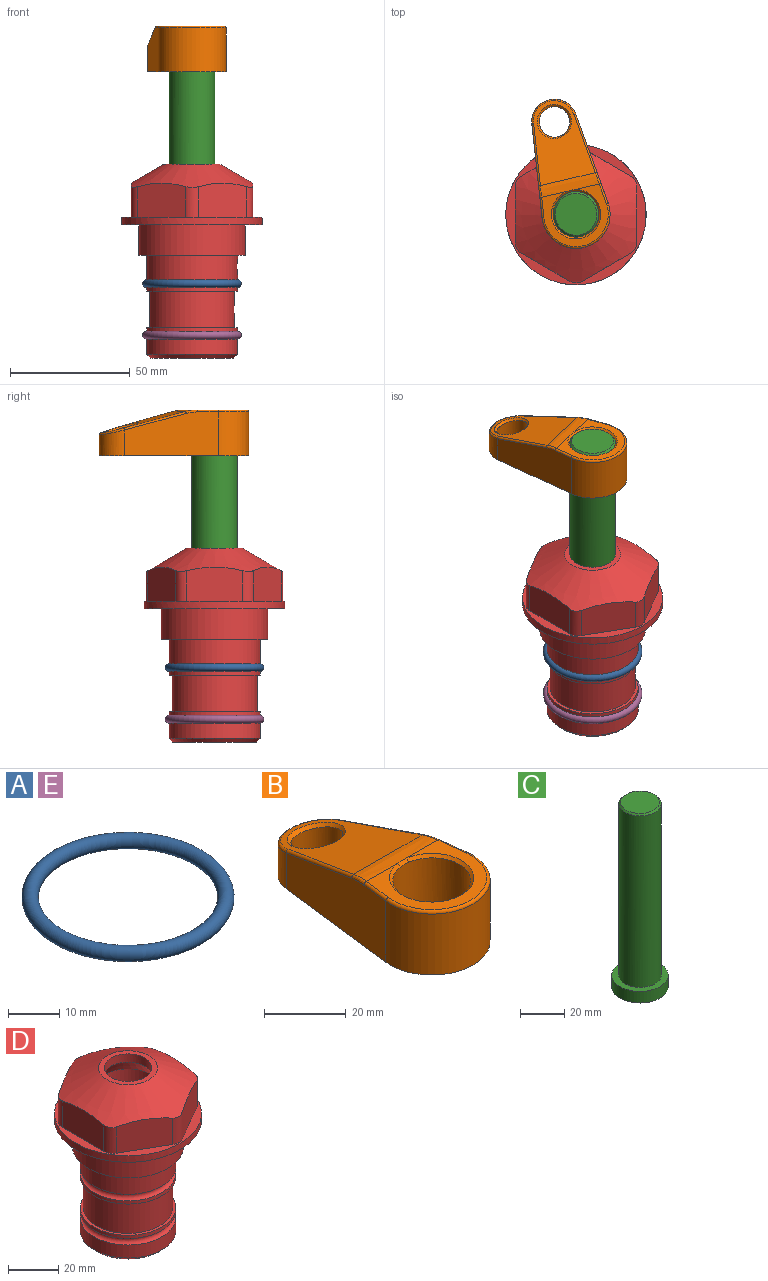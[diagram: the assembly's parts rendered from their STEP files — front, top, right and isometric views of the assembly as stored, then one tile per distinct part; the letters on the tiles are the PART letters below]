
ASSEMBLY  parts=5 mates=4
PART A: 1 faces, bbox 44.7x44.7x3.2 mm
  f0: torus R=19.05mm, axis (0,0,1), area 1193.9mm2
PART B: 31 faces, bbox 31.7x65.5x19.8 mm
  f0: plane 39.12x18.26mm, normal (0.99,0.12,0), area 612.2mm2, adj f1,f4,f7,f11,f13,f15
  f1: cylinder r=9.53mm len=18.91mm, axis (0,0,-1), area 296.1mm2, adj f0,f2,f7,f17
  f2: plane 39.12x18.26mm, normal (-0.99,0.12,0), area 612.2mm2, adj f1,f4,f7,f12,f14,f16
  f3: cylinder r=6.35mm len=12.7mm, axis (0,0,-1), area 362.4mm2, adj f7,f18
  f4: cylinder r=14.29mm len=28.58mm, axis (0,0,-1), area 882.2mm2, adj f0,f2,f7,f10
  f5: cylinder r=9.53mm len=19.05mm, axis (0,0,-1), area 1092.6mm2, adj f7,f19,f20
  f6: plane 26.99x23.69mm, normal (0,0,1), area 216.2mm2, adj f9,f10,f11,f12,f19
  f7: plane 63.5x28.58mm, normal (0,0,-1), area 661.8mm2, adj f0,f1,f2,f3,f4,f5,f22,f23
  f8: plane 33.52x23.6mm, normal (0,0.26,0.97), area 486mm2, adj f9,f15,f16,f17,f18
  f9: cylinder r=19.05mm len=24.72mm, axis (1,0,0), area 120.4mm2, adj f6,f8,f13,f14,f20
  f10: torus R=13.49mm, axis (0,0,1), area 59mm2, adj f4,f6,f11,f12
  f11: cylinder r=0.79mm len=8.67mm, axis (0.12,-0.99,0), area 10.8mm2, adj f0,f6,f10,f13
  f12: cylinder r=0.79mm len=8.67mm, axis (0.12,0.99,0), area 10.8mm2, adj f2,f6,f10,f14
  f13: bspline ~4.95x1.42mm, area 6.1mm2, adj f0,f9,f11,f15
  f14: bspline ~4.95x1.42mm, area 6.1mm2, adj f2,f9,f12,f16
  f15: cylinder r=0.79mm len=25.95mm, axis (0.12,-0.96,0.26), area 32.9mm2, adj f0,f8,f13,f17
  f16: cylinder r=0.79mm len=25.95mm, axis (0.12,0.96,-0.26), area 32.9mm2, adj f2,f8,f14,f17
  f17: bspline ~18.91x8.38mm, area 30mm2, adj f1,f8,f15,f16
  f18: bspline ~14.29x14.29mm, area 48.3mm2, adj f3,f8
  f19: cone r=9.53mm half-angle=45deg, axis (0,0,1), area 66.5mm2, adj f5,f6,f20
  f20: bspline ~3.22x0.96mm, area 3.5mm2, adj f5,f9,f19
  f21: plane 2.75x2.72mm, normal (0,0,-1), area 2.9mm2, adj f23,f25,f28
  f22: plane 23.05x15.88mm, normal (-0.99,-0.12,0), area 323.6mm2, adj f7,f25,f26,f27,f28,f29
  f23: plane 23.05x15.88mm, normal (0.99,-0.12,0), area 323.6mm2, adj f7,f21,f25,f27,f28,f30
  f24: cylinder r=9.53mm len=10.69mm, axis (0,0,-1), area 114.7mm2, adj f7,f27,f29,f30
  f25: cylinder r=12.7mm len=20.59mm, axis (0,0,-1), area 381.1mm2, adj f7,f21,f22,f23,f26,f28
  f26: plane 2.75x2.72mm, normal (0,0,-1), area 2.9mm2, adj f22,f25,f28
  f27: plane 19.72x18.37mm, normal (0,-0.26,-0.97), area 291.8mm2, adj f22,f23,f24,f28,f29,f30
  f28: cylinder r=15.88mm len=19.92mm, axis (1,0,0), area 54.8mm2, adj f21,f22,f23,f25,f26,f27
  f29: cylinder r=1.59mm len=11mm, axis (0,0,-1), area 34.7mm2, adj f7,f22,f24,f27
  f30: cylinder r=1.59mm len=11mm, axis (0,0,-1), area 34.7mm2, adj f7,f23,f24,f27
PART C: 6 faces, bbox 25.4x25.4x101.6 mm
  f0: plane 17.46x17.46mm, normal (0,0,1), area 239.5mm2, adj f5
  f1: plane 25.4x25.4mm, normal (0,0,-1), area 506.7mm2, adj f2
  f2: cylinder r=12.7mm len=25.4mm, axis (0,0,1), area 506.7mm2, adj f1,f3
  f3: plane 25.4x25.4mm, normal (0,0,1), area 221.7mm2, adj f2,f4
  f4: cylinder r=9.53mm len=94.46mm, axis (0,0,1), area 5653mm2, adj f3,f5
  f5: cone r=8.73mm half-angle=45deg, axis (0,0,-1), area 64.4mm2, adj f0,f4
PART D: 36 faces, bbox 58.7x58.7x81 mm
  f0: cylinder r=17.78mm len=35.56mm, axis (0,0,1), area 1670.8mm2, adj f23,f24,f31
  f1: cylinder r=19.05mm len=38.1mm, axis (0,0,1), area 1191.9mm2, adj f26,f27,f30
  f2: plane 58.66x58.66mm, normal (0,0,-1), area 1150.6mm2, adj f3,f28
  f3: cylinder r=29.33mm len=58.66mm, axis (0,0,-1), area 585.1mm2, adj f2,f4
  f4: plane 58.66x58.66mm, normal (0,0,1), area 475.9mm2, adj f3,f5,f6,f7,f8,f9,f10,f11
  f5: plane 20.32x14.34mm, normal (-0.5,0.87,0), area 324.4mm2, adj f4,f15,f16,f17
  f6: plane 20.32x14.34mm, normal (0.5,0.87,0), area 324.4mm2, adj f4,f14,f15,f17
  f7: plane 23.48x14.34mm, normal (1,0,0), area 324.4mm2, adj f4,f13,f14,f17
  f8: plane 20.32x14.34mm, normal (0.5,-0.87,0), area 324.4mm2, adj f4,f12,f13,f17
  f9: plane 20.32x14.34mm, normal (-0.5,-0.87,0), area 324.4mm2, adj f4,f11,f12,f17
  f10: plane 23.48x14.34mm, normal (-1,0,0), area 324.4mm2, adj f4,f11,f16,f17
  f11: cylinder r=5.08mm len=12.85mm, axis (0,0,-1), area 67.2mm2, adj f4,f9,f10,f17
  f12: cylinder r=5.08mm len=12.85mm, axis (0,0,-1), area 67.2mm2, adj f4,f8,f9,f17
  f13: cylinder r=5.08mm len=12.85mm, axis (0,0,-1), area 67.2mm2, adj f4,f7,f8,f17
  f14: cylinder r=5.08mm len=12.85mm, axis (0,0,-1), area 67.2mm2, adj f4,f6,f7,f17
  f15: cylinder r=5.08mm len=12.85mm, axis (0,0,-1), area 67.2mm2, adj f4,f5,f6,f17
  f16: cylinder r=5.08mm len=12.85mm, axis (0,0,-1), area 67.2mm2, adj f4,f5,f10,f17
  f17: cone r=11.73mm half-angle=60deg, axis (0,0,-1), area 2071.8mm2, adj f5,f6,f7,f8,f9,f10,f11,f12
  f18: plane 23.46x23.46mm, normal (0,0,1), area 147.4mm2, adj f17,f35
  f19: plane 34.93x34.93mm, normal (0,0,-1), area 958mm2, adj f29
  f20: cylinder r=19.05mm len=38.1mm, axis (0,0,1), area 760.1mm2, adj f21,f29
  f21: torus R=19.05mm, axis (0,0,1), area 565.3mm2, adj f20,f22
  f22: cylinder r=19.05mm len=38.1mm, axis (0,0,1), area 190mm2, adj f21,f23
  f23: plane 38.1x38.1mm, normal (0,0,1), area 146.9mm2, adj f0,f22
  f24: plane 38.1x38.1mm, normal (0,0,-1), area 146.9mm2, adj f0,f25
  f25: cylinder r=19.05mm len=38.1mm, axis (0,0,1), area 190mm2, adj f24,f26
  f26: torus R=19.05mm, axis (0,0,1), area 565.3mm2, adj f1,f25
  f27: plane 44.45x44.45mm, normal (0,0,-1), area 411.7mm2, adj f1,f28
  f28: cylinder r=22.23mm len=44.45mm, axis (0,0,1), area 1773.5mm2, adj f2,f27
  f29: cone r=19.05mm half-angle=45deg, axis (0,0,1), area 257.5mm2, adj f19,f20
  f30: cylinder r=3.17mm len=6.75mm, axis (-1,0,0), area 128mm2, adj f1,f33
  f31: cylinder r=3.17mm len=6.35mm, axis (-1,0,0), area 102.5mm2, adj f0,f33
  f32: plane 25.4x25.4mm, normal (0,0,1), area 506.7mm2, adj f33
  f33: cylinder r=12.7mm len=66.42mm, axis (0,0,-1), area 5236.2mm2, adj f30,f31,f32,f34
  f34: cone r=9.53mm half-angle=30deg, axis (0,0,-1), area 443.4mm2, adj f33,f35
  f35: cylinder r=9.53mm len=19.05mm, axis (0,0,-1), area 240.9mm2, adj f18,f34
PART E: same geometry as A
PLACE A at identity
PLACE B rot(axis=(0,0,1),13.1deg) t=(0,0,19.73)mm
PLACE C rot(axis=(0,0,1),13.1deg) t=(0,0,19.73)mm
PLACE D at identity fixed
PLACE E t=(0,0,-21.59)mm
MATE fastened E.f0 <-> D.f0  axis (0,0,1) through (0,0,-46.1)mm
MATE cylindrical C.f2 <-> D.f0  axis (0,0,-1) through (0,0,-18.37)mm
MATE fastened B.f4 <-> C.f2  axis (0,0,1) through (0,0,83.23)mm
MATE fastened A.f0 <-> D.f0  axis (0,0,1) through (0,0,-24.51)mm
